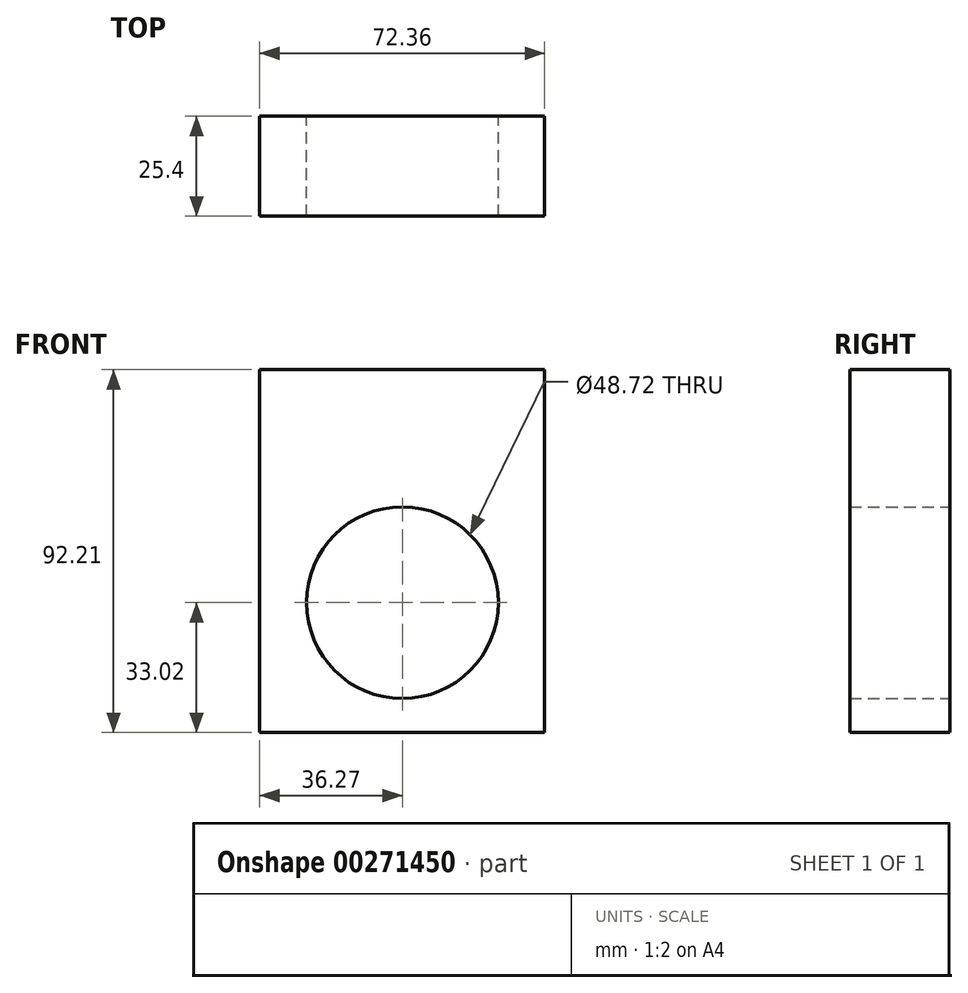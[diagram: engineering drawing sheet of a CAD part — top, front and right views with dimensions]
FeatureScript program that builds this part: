
annotation { "Feature Type Name" : "Feature", "Feature Type Description" : "" }
export const myFeature = defineFeature(function(context is Context, id is Id, definition is map)
    precondition{}
    {
        {
            var Q0;
            Q0=qCreatedBy(makeId("Front.planeOp"),FACE);
            var sketch = newSketch(context, id + "F0", { "sketchPlane" : qUnion([Q0])});
            skCircle(sketch, "E0", {"center": v(0, 0) * mm, "radius": 24.36 * mm});
            skLineSegment(sketch, "E1.bottom", {"start": v(-36.27, 59.19) * mm, "end": v(36.09, 59.19) * mm});
            skLineSegment(sketch, "E1.top", {"start": v(-36.27, -33.02) * mm, "end": v(36.09, -33.02) * mm});
            skLineSegment(sketch, "E1.left", {"start": v(-36.27, 59.19) * mm, "end": v(-36.27, -33.02) * mm});
            skLineSegment(sketch, "E1.right", {"start": v(36.09, 59.19) * mm, "end": v(36.09, -33.02) * mm});
            skSolve(sketch);
        }
        {
            var Q0;
            Q0=makeQuery(id+"F0.imprint","IMPRINT",FACE,{"disambiguationData":[TD([[makeQuery(id+"F0.imprint","IMPRINT",EDGE,{"derivedFrom":sQuery(id+"F0.wireOp",EDGE,"E0")}),-1.0]])]});
            extrude(context, id + "F1", {"entities" : qUnion([Q0]), "depth" : 25.4 * mm});
        }
    });
